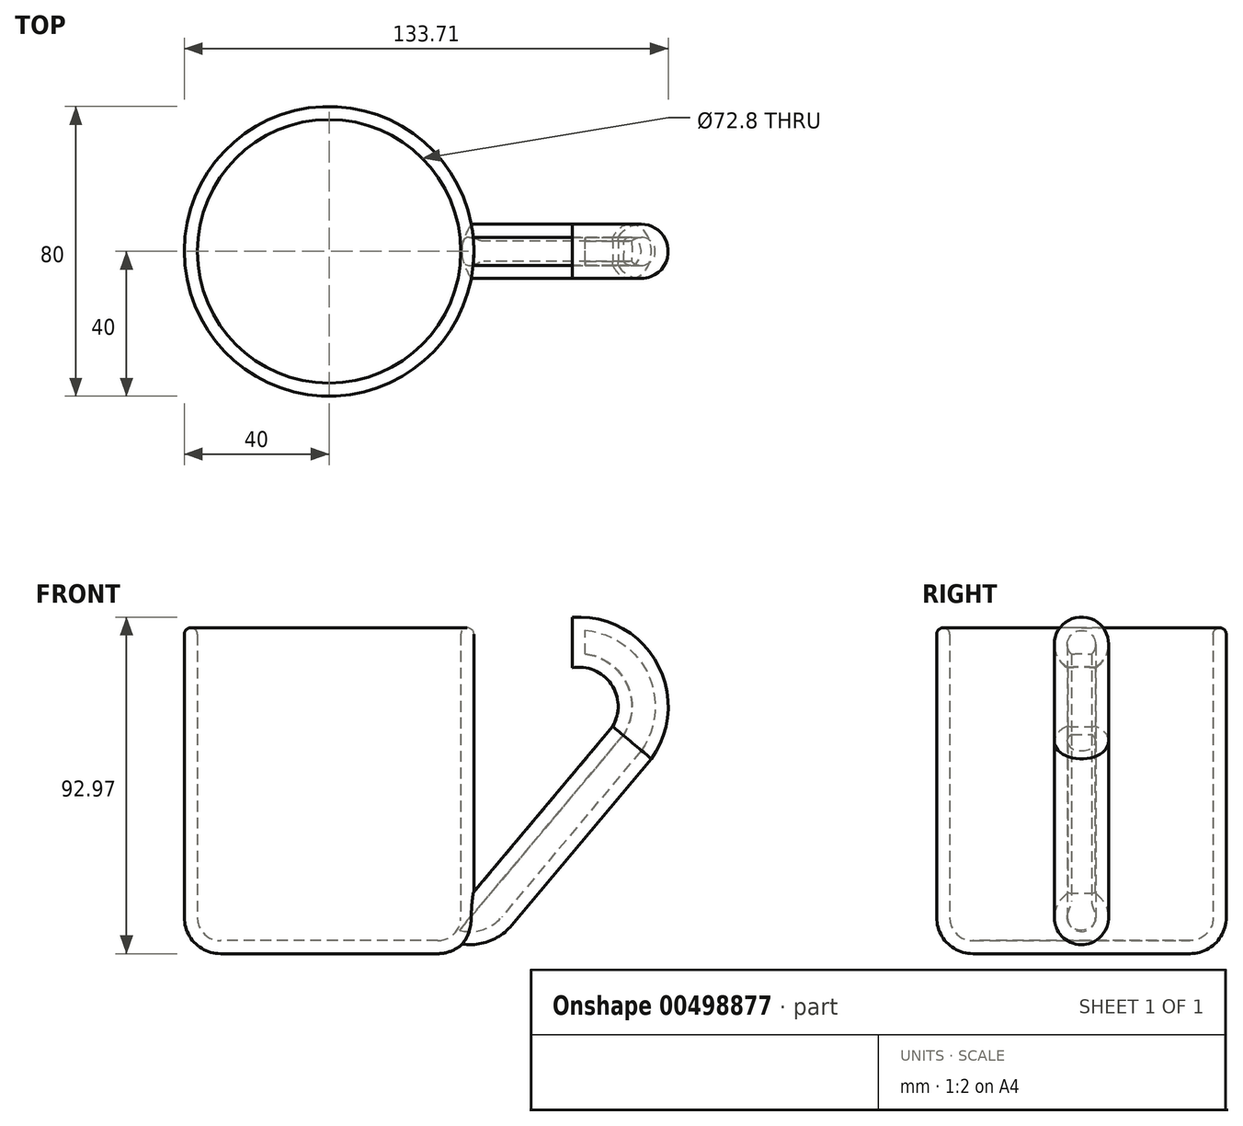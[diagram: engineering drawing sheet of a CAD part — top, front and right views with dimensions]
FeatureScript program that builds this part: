
annotation { "Feature Type Name" : "Feature", "Feature Type Description" : "" }
export const myFeature = defineFeature(function(context is Context, id is Id, definition is map)
    precondition{}
    {
        {
            var Q0;
            Q0=qCreatedBy(makeId("Top.planeOp"),FACE);
            var sketch = newSketch(context, id + "F0", { "sketchPlane" : qUnion([Q0])});
            skCircle(sketch, "E0", {"center": v(0, 0) * mm, "radius": 40 * mm});
            skSolve(sketch);
        }
        {
            var Q0;
            Q0 = qSketchRegion(id + "F0", true);
            extrude(context, id + "F1", {"entities" : qUnion([Q0]), "depth" : 90 * mm});
        }
        {
            var Q0;
            Q0=qCreatedBy(makeId("Right.planeOp"),FACE);
            cPlane(context, id + "F2", {"entities" : qUnion([Q0]), "cplaneType" : CPlaneType.OFFSET, "offset" : 39 * mm, "width" : 150 * mm, "height" : 150 * mm});
        }
        {
            var Q0;
            Q0=qCreatedBy(id+"F2.planeOp",FACE);
            var sketch = newSketch(context, id + "F3", { "sketchPlane" : qUnion([Q0])});
            skCircle(sketch, "E1", {"center": v(0, 10) * mm, "radius": 7.5 * mm});
            skLineSegment(sketch, "E2", {"start": v(0, 17.5) * mm, "end": v(42.75, 17.5) * mm});
            skLineSegment(sketch, "E3", {"start": v(42.75, 17.5) * mm, "end": v(-70.7, 17.5) * mm});
            skPoint(sketch, "E3.endSnap0", {"position": v(21.38, 17.5) * mm});
            skSolve(sketch);
        }
        {
            var Q0;
            Q0 = qSketchRegion(id + "F3", true);
            var Q1;
            Q1=sQuery(id+"F3.wireOp",EDGE,"E3");
            revolve(context, id + "F4", {"operationType" : NewBodyOperationType.ADD, "entities" : qUnion([Q0]), "axis" : qUnion([Q1]), "revolveType" : RevolveType.ONE_DIRECTION, "angle" : 50 * degree});
        }
        {
            var Q0;
            Q0=makeQuery(id+"F4.opRevolve","CAP_FACE",FACE,{"disambiguationData":[OSD([sQuery(id+"F3.wireOp",EDGE,"E1")])],"isStart":false});
            extrude(context, id + "F5", {"entities" : qUnion([Q0]), "operationType" : NewBodyOperationType.ADD, "depth" : 60 * mm});
        }
        {
            var Q0;
            Q0=qCreatedBy(makeId("Right.planeOp"),FACE);
            cPlane(context, id + "F6", {"entities" : qUnion([Q0]), "cplaneType" : CPlaneType.OFFSET, "offset" : 69 * mm, "width" : 150 * mm, "height" : 150 * mm});
        }
        {
            var Q0;
            Q0=qCreatedBy(id+"F6.planeOp",FACE);
            var sketch = newSketch(context, id + "F7", { "sketchPlane" : qUnion([Q0])});
            skLineSegment(sketch, "E4", {"start": v(0, 68.26) * mm, "end": v(35.22, 68.26) * mm});
            skLineSegment(sketch, "E5", {"start": v(35.22, 68.26) * mm, "end": v(-50.19, 68.26) * mm});
            skSolve(sketch);
        }
        {
            var Q0;
            Q0=makeQuery(id+"F5.opExtrude","CAP_FACE",FACE,{"disambiguationData":[OSD([sQuery(id+"F3.wireOp",EDGE,"E1")])],"isStart":false});
            var Q1;
            Q1=sQuery(id+"F7.wireOp",EDGE,"E5");
            revolve(context, id + "F8", {"operationType" : NewBodyOperationType.ADD, "entities" : qUnion([Q0]), "axis" : qUnion([Q1]), "revolveType" : RevolveType.ONE_DIRECTION, "angle" : 130 * degree});
        }
        {
            var Q0;
            Q0=makeQuery(id+"F1.opExtrude","CAP_EDGE",EDGE,{"disambiguationData":[OSD([sQuery(id+"F0.wireOp",EDGE,"E0")])],"isStart":true});
            fillet(context, id + "F9", {"entities" : qUnion([Q0]), "radius" : 10 * mm, "tangentPropagation" : true, "allowEdgeOverflow" : false});
        }
        {
            var Q0;
            Q0=makeQuery(id+"F1.opExtrude","CAP_FACE",FACE,{"disambiguationData":[OSD([sQuery(id+"F0.wireOp",EDGE,"E0")])],"isStart":false});
            shell(context, id + "F10", {"entities" : qUnion([Q0]), "thickness" : 3.6 * mm});
        }
        {
            var Q0;
            {var subQ0=sQuery(id+"F0.wireOp",EDGE,"E0");Q0=makeQuery(id+"F10.opShell","OFFSET_EDGE",EDGE,{"disambiguationData":[OSD([subQ0]),TDD([makeQuery(id+"F1.opExtrude","CAP_EDGE",EDGE,{"disambiguationData":[OSD([subQ0])],"isStart":false})])]});}
            var Q1;
            Q1=makeQuery(id+"F1.opExtrude","CAP_EDGE",EDGE,{"disambiguationData":[OSD([sQuery(id+"F0.wireOp",EDGE,"E0")])],"isStart":false});
            fillet(context, id + "F11", {"entities" : qUnion([Q0, Q1]), "radius" : 1.8 * mm, "tangentPropagation" : true, "allowEdgeOverflow" : false});
        }
    });
